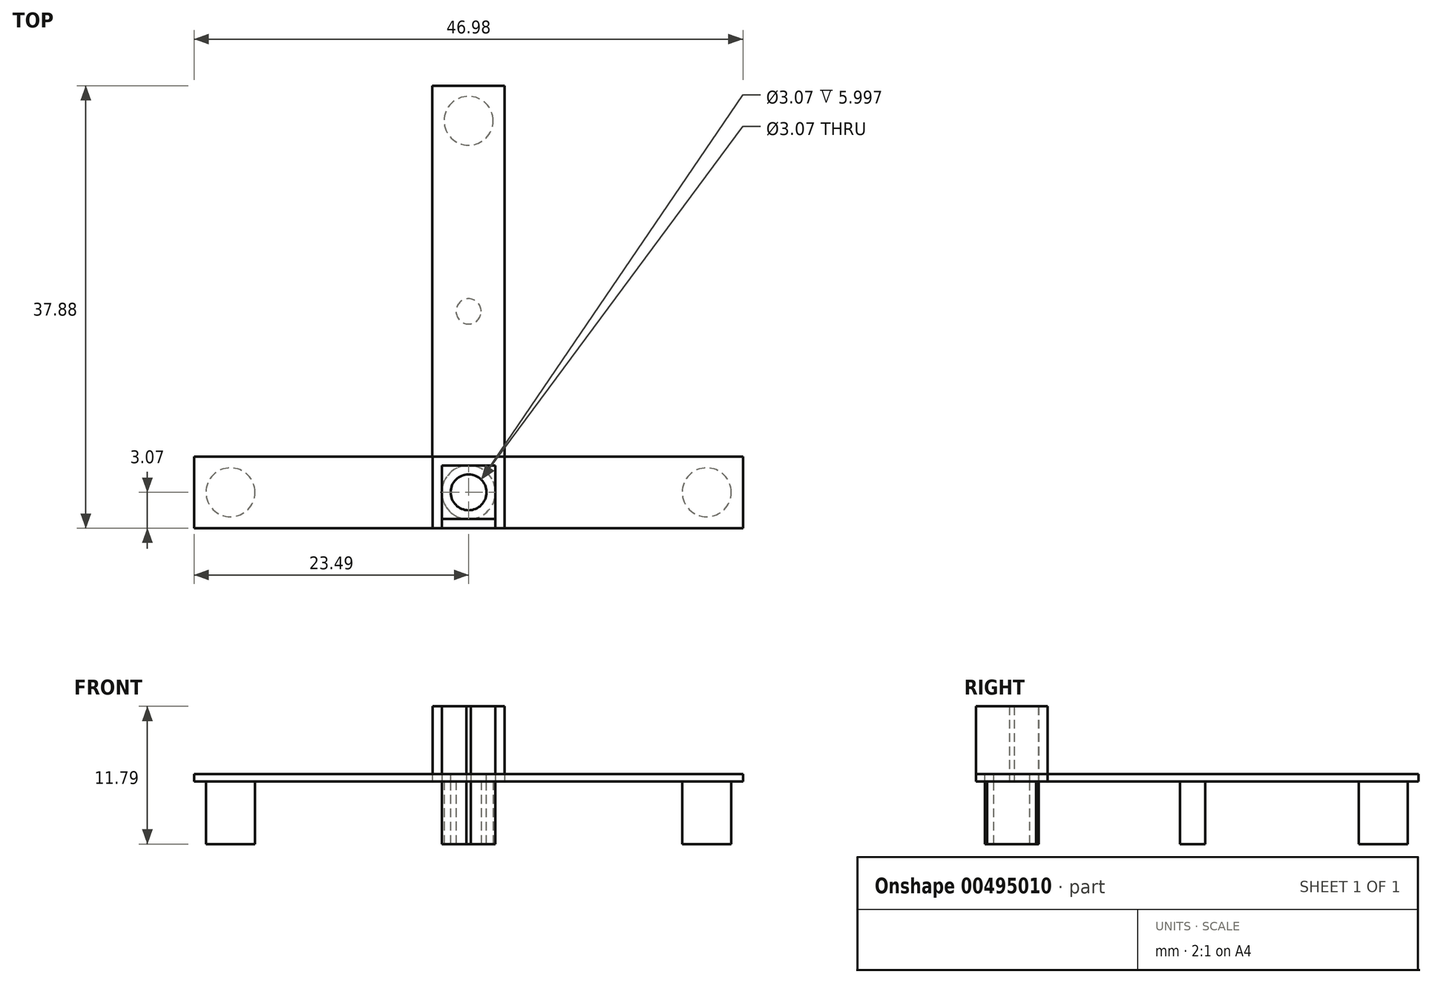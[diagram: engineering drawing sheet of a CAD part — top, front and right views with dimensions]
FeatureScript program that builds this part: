
annotation { "Feature Type Name" : "Feature", "Feature Type Description" : "" }
export const myFeature = defineFeature(function(context is Context, id is Id, definition is map)
    precondition{}
    {
        {
            var Q0;
            Q0=qCreatedBy(makeId("Top.planeOp"),FACE);
            var sketch = newSketch(context, id + "F0", { "sketchPlane" : qUnion([Q0])});
            skCircle(sketch, "E0", {"center": v(0, 0) * mm, "radius": 1.52 * mm});
            skCircle(sketch, "E1", {"center": v(0, 0) * mm, "radius": 2.3 * mm});
            skSolve(sketch);
        }
        {
            var Q0;
            Q0 = qSketchRegion(id + "F0", true);
            extrude(context, id + "F1", {"entities" : qUnion([Q0]), "depth" : 6 * mm});
        }
        {
            var Q0;
            Q0=makeQuery(id+"F1.opExtrude","CAP_FACE",FACE,{"disambiguationData":[OSD([sQuery(id+"F0.wireOp",EDGE,"E0"),sQuery(id+"F0.wireOp",EDGE,"E1")])],"isStart":false});
            var sketch = newSketch(context, id + "F2", { "sketchPlane" : qUnion([Q0])});
            skPoint(sketch, "E2.middle", {"position": v(0, 0) * mm});
            skLineSegment(sketch, "E3.bottom", {"start": v(2.3, 2.3) * mm, "end": v(-2.3, 2.3) * mm});
            skLineSegment(sketch, "E3.top", {"start": v(2.3, -2.3) * mm, "end": v(-2.3, -2.3) * mm});
            skLineSegment(sketch, "E3.left", {"start": v(2.3, 2.3) * mm, "end": v(2.3, -2.3) * mm});
            skLineSegment(sketch, "E3.right", {"start": v(-2.3, 2.3) * mm, "end": v(-2.3, -2.3) * mm});
            skCircle(sketch, "E4", {"center": v(0, 0) * mm, "radius": 1.52 * mm});
            skSolve(sketch);
        }
        {
            var Q0;
            Q0 = qSketchRegion(id + "F2", true);
            extrude(context, id + "F3", {"entities" : qUnion([Q0]), "operationType" : NewBodyOperationType.ADD, "oppositeDirection" : true, "depth" : 0.64 * mm});
        }
        {
            var Q0;
            Q0=makeQuery(id+"F3.boolean.opBoolean","MERGE",FACE,{"derivedFrom":[makeQuery(id+"F1.opExtrude","CAP_FACE",FACE,{"disambiguationData":[OSD([sQuery(id+"F0.wireOp",EDGE,"E0"),sQuery(id+"F0.wireOp",EDGE,"E1")])],"isStart":false}),makeQuery(id+"F3.opExtrude","CAP_FACE",FACE,{"disambiguationData":[OSD([sQuery(id+"F2.wireOp",EDGE,"E3.bottom"),sQuery(id+"F2.wireOp",EDGE,"E3.top"),sQuery(id+"F2.wireOp",EDGE,"E3.left"),sQuery(id+"F2.wireOp",EDGE,"E3.right"),sQuery(id+"F2.wireOp",EDGE,"E4")])],"isStart":true})]});
            var sketch = newSketch(context, id + "F4", { "sketchPlane" : qUnion([Q0])});
            skLineSegment(sketch, "E5.bottom", {"start": v(2.3, 2.3) * mm, "end": v(-2.3, 2.3) * mm});
            skLineSegment(sketch, "E5.top", {"start": v(2.3, -2.3) * mm, "end": v(-2.3, -2.3) * mm});
            skLineSegment(sketch, "E5.left", {"start": v(2.3, 2.3) * mm, "end": v(2.3, -2.3) * mm});
            skLineSegment(sketch, "E5.right", {"start": v(-2.3, 2.3) * mm, "end": v(-2.3, -2.3) * mm});
            skPoint(sketch, "E5.middle", {"position": v(0, 0) * mm});
            skLineSegment(sketch, "E6.bottom", {"start": v(3.07, 3.07) * mm, "end": v(-3.07, 3.07) * mm});
            skLineSegment(sketch, "E6.top", {"start": v(3.07, -3.07) * mm, "end": v(-3.07, -3.07) * mm});
            skLineSegment(sketch, "E6.left", {"start": v(3.07, 3.07) * mm, "end": v(3.07, -3.07) * mm});
            skLineSegment(sketch, "E6.right", {"start": v(-3.07, 3.07) * mm, "end": v(-3.07, -3.07) * mm});
            skSolve(sketch);
        }
        {
            var Q0;
            Q0=makeQuery(id+"F4.imprint","IMPRINT",FACE,{"disambiguationData":[TD([[makeQuery(id+"F4.imprint","IMPRINT",EDGE,{"derivedFrom":sQuery(id+"F4.wireOp",EDGE,"E6.bottom")}),1.0]])]});
            extrude(context, id + "F5", {"entities" : qUnion([Q0]), "depth" : 5.8 * mm});
        }
        {
            var Q0;
            Q0=makeQuery(id+"F5.opExtrude","CAP_FACE",FACE,{"disambiguationData":[OSD([sQuery(id+"F0.wireOp",EDGE,"E1"),sQuery(id+"F4.wireOp",EDGE,"E5.bottom"),sQuery(id+"F4.wireOp",EDGE,"E5.top"),sQuery(id+"F4.wireOp",EDGE,"E5.left"),sQuery(id+"F4.wireOp",EDGE,"E5.right"),sQuery(id+"F4.wireOp",EDGE,"E6.bottom"),sQuery(id+"F4.wireOp",EDGE,"E6.top"),sQuery(id+"F4.wireOp",EDGE,"E6.left"),sQuery(id+"F4.wireOp",EDGE,"E6.right")])],"isStart":false});
            var sketch = newSketch(context, id + "F6", { "sketchPlane" : qUnion([Q0])});
            skLineSegment(sketch, "E7.bottom", {"start": v(-2.3, -2.3) * mm, "end": v(2.29, -2.3) * mm});
            skLineSegment(sketch, "E7.top", {"start": v(-2.3, -4.61) * mm, "end": v(2.29, -4.61) * mm});
            skLineSegment(sketch, "E7.left", {"start": v(-2.3, -2.3) * mm, "end": v(-2.3, -4.61) * mm});
            skLineSegment(sketch, "E7.right", {"start": v(2.29, -2.3) * mm, "end": v(2.29, -4.61) * mm});
            skSolve(sketch);
        }
        {
            var Q0;
            Q0 = qSketchRegion(id + "F6", true);
            extrude(context, id + "F7", {"entities" : qUnion([Q0]), "operationType" : NewBodyOperationType.REMOVE, "oppositeDirection" : true, "depth" : 25.4 * mm});
        }
        {
            var Q0;
            Q0=makeQuery(id+"F3.boolean.opBoolean","MERGE",FACE,{"derivedFrom":[makeQuery(id+"F1.opExtrude","CAP_FACE",FACE,{"disambiguationData":[OSD([sQuery(id+"F0.wireOp",EDGE,"E0"),sQuery(id+"F0.wireOp",EDGE,"E1")])],"isStart":false}),makeQuery(id+"F3.opExtrude","CAP_FACE",FACE,{"disambiguationData":[OSD([sQuery(id+"F2.wireOp",EDGE,"E3.bottom"),sQuery(id+"F2.wireOp",EDGE,"E3.top"),sQuery(id+"F2.wireOp",EDGE,"E3.left"),sQuery(id+"F2.wireOp",EDGE,"E3.right"),sQuery(id+"F2.wireOp",EDGE,"E4")])],"isStart":true})]});
            var sketch = newSketch(context, id + "F8", { "sketchPlane" : qUnion([Q0])});
            skLineSegment(sketch, "E8.bottom", {"start": v(23.5, 3.06) * mm, "end": v(-23.5, 3.06) * mm});
            skLineSegment(sketch, "E8.top", {"start": v(23.5, -3.06) * mm, "end": v(-23.5, -3.06) * mm});
            skLineSegment(sketch, "E8.left", {"start": v(23.5, 3.06) * mm, "end": v(23.5, -3.06) * mm});
            skLineSegment(sketch, "E8.right", {"start": v(-23.5, 3.06) * mm, "end": v(-23.5, -3.06) * mm});
            skPoint(sketch, "E8.middle", {"position": v(0, 0) * mm});
            skSolve(sketch);
        }
        {
            var Q0;
            Q0 = qSketchRegion(id + "F8", true);
            extrude(context, id + "F9", {"entities" : qUnion([Q0]), "oppositeDirection" : true, "depth" : 0.64 * mm});
        }
        {
            var Q0;
            Q0=makeQuery(id+"F9.opExtrude","CAP_FACE",FACE,{"disambiguationData":[OSD([sQuery(id+"F8.wireOp",EDGE,"E8.bottom"),sQuery(id+"F8.wireOp",EDGE,"E8.top"),sQuery(id+"F8.wireOp",EDGE,"E8.left"),sQuery(id+"F8.wireOp",EDGE,"E8.right")])],"isStart":true});
            var sketch = newSketch(context, id + "F10", { "sketchPlane" : qUnion([Q0])});
            skLineSegment(sketch, "E9.bottom", {"start": v(3.06, 34.3) * mm, "end": v(-3.06, 34.3) * mm});
            skLineSegment(sketch, "E9.top", {"start": v(3.06, -34.3) * mm, "end": v(-3.06, -34.3) * mm});
            skLineSegment(sketch, "E9.left", {"start": v(3.06, 34.3) * mm, "end": v(3.06, -34.3) * mm});
            skLineSegment(sketch, "E9.right", {"start": v(-3.06, 34.3) * mm, "end": v(-3.06, -34.3) * mm});
            skPoint(sketch, "E9.middle", {"position": v(0, 0) * mm});
            skSolve(sketch);
        }
        {
            var Q0;
            {var subQ0=sQuery(id+"F10.wireOp",EDGE,"E9.left");var subQ1=makeQuery(id+"F9.opExtrude","CAP_EDGE",EDGE,{"disambiguationData":[OSD([sQuery(id+"F8.wireOp",EDGE,"E8.bottom")])],"isStart":true});var subQ2=makeQuery(id+"F10.imprint","INTERSECT",VERTEX,{"derivedFrom":[subQ1,subQ0]});Q0=makeQuery(id+"F10.imprint","IMPRINT",FACE,{"disambiguationData":[TD([[makeQuery(id+"F10.imprint","IMPRINT",EDGE,{"disambiguationData":[TD([[subQ2,-1.0]])],"derivedFrom":subQ0}),-1.0]])]});}
            var Q1;
            {var subQ0=sQuery(id+"F10.wireOp",EDGE,"E9.bottom");Q1=makeQuery(id+"F10.imprint","IMPRINT",FACE,{"disambiguationData":[TD([[makeQuery(id+"F10.imprint","IMPRINT",EDGE,{"derivedFrom":subQ0}),1.0]])]});}
            var Q2;
            {var subQ0=sQuery(id+"F10.wireOp",EDGE,"E9.top");Q2=makeQuery(id+"F10.imprint","IMPRINT",FACE,{"disambiguationData":[TD([[makeQuery(id+"F10.imprint","IMPRINT",EDGE,{"derivedFrom":subQ0}),-1.0]])]});}
            extrude(context, id + "F11", {"entities" : qUnion([Q0, Q1, Q2]), "oppositeDirection" : true, "depth" : 0.64 * mm});
        }
        {
            var Q0;
            Q0=makeQuery(id+"F11.opExtrude","CAP_FACE",FACE,{"disambiguationData":[OSD([sQuery(id+"F10.wireOp",EDGE,"E9.bottom"),sQuery(id+"F10.wireOp",EDGE,"E9.top"),sQuery(id+"F10.wireOp",EDGE,"E9.left"),sQuery(id+"F10.wireOp",EDGE,"E9.right")])],"isStart":true});
            var sketch = newSketch(context, id + "F12", { "sketchPlane" : qUnion([Q0])});
            skLineSegment(sketch, "E10.bottom", {"start": v(-3.06, -3.07) * mm, "end": v(3.06, -3.07) * mm});
            skLineSegment(sketch, "E10.top", {"start": v(-3.06, -34.3) * mm, "end": v(3.06, -34.3) * mm});
            skLineSegment(sketch, "E10.left", {"start": v(-3.06, -3.07) * mm, "end": v(-3.06, -34.3) * mm});
            skLineSegment(sketch, "E10.right", {"start": v(3.06, -3.07) * mm, "end": v(3.06, -34.3) * mm});
            skSolve(sketch);
        }
        {
            var Q0;
            Q0 = qSketchRegion(id + "F12", true);
            extrude(context, id + "F13", {"entities" : qUnion([Q0]), "operationType" : NewBodyOperationType.REMOVE, "oppositeDirection" : true, "depth" : 25.4 * mm});
        }
        {
            var Q0;
            Q0=makeQuery(id+"F11.opExtrude","SWEPT_BODY",BODY,{"disambiguationData":[OSD([sQuery(id+"F10.wireOp",EDGE,"E9.bottom"),sQuery(id+"F10.wireOp",EDGE,"E9.top"),sQuery(id+"F10.wireOp",EDGE,"E9.left"),sQuery(id+"F10.wireOp",EDGE,"E9.right")])]});
            deleteBodies(context, id + "F14", {"entities" : qUnion([Q0])});
        }
        {
            var Q0;
            Q0=makeQuery(id+"F9.opExtrude","SWEPT_FACE",FACE,{"disambiguationData":[OSD([sQuery(id+"F8.wireOp",EDGE,"E8.bottom")])]});
            var sketch = newSketch(context, id + "F15", { "sketchPlane" : qUnion([Q0])});
            skLineSegment(sketch, "E11.bottom", {"start": v(3.1, 6) * mm, "end": v(-3.07, 6) * mm});
            skLineSegment(sketch, "E11.top", {"start": v(3.1, 5.36) * mm, "end": v(-3.07, 5.36) * mm});
            skLineSegment(sketch, "E11.left", {"start": v(3.1, 6) * mm, "end": v(3.1, 5.36) * mm});
            skLineSegment(sketch, "E11.right", {"start": v(-3.07, 6) * mm, "end": v(-3.07, 5.36) * mm});
            skSolve(sketch);
        }
        {
            var Q0;
            Q0 = qSketchRegion(id + "F15", true);
            extrude(context, id + "F16", {"entities" : qUnion([Q0]), "depth" : 31.75 * mm});
        }
        {
            var Q0;
            Q0=makeQuery(id+"F9.opExtrude","CAP_FACE",FACE,{"disambiguationData":[OSD([sQuery(id+"F8.wireOp",EDGE,"E8.bottom"),sQuery(id+"F8.wireOp",EDGE,"E8.top"),sQuery(id+"F8.wireOp",EDGE,"E8.left"),sQuery(id+"F8.wireOp",EDGE,"E8.right")])],"isStart":true});
            var sketch = newSketch(context, id + "F17", { "sketchPlane" : qUnion([Q0])});
            skCircle(sketch, "E12", {"center": v(0, 0) * mm, "radius": 1.53 * mm});
            skSolve(sketch);
        }
        {
            var Q0;
            Q0 = qSketchRegion(id + "F17", true);
            extrude(context, id + "F18", {"entities" : qUnion([Q0]), "operationType" : NewBodyOperationType.REMOVE, "oppositeDirection" : true, "depth" : 25.4 * mm});
        }
        {
            var Q0;
            Q0=qCreatedBy(makeId("Top.planeOp"),FACE);
            var sketch = newSketch(context, id + "F19", { "sketchPlane" : qUnion([Q0])});
            skCircle(sketch, "E13", {"center": v(-20.38, 0) * mm, "radius": 2.1 * mm});
            skCircle(sketch, "E14", {"center": v(0, 31.8) * mm, "radius": 2.1 * mm});
            skCircle(sketch, "E15.MirrorC", {"center": v(20.38, 0) * mm, "radius": 2.1 * mm});
            skCircle(sketch, "E16", {"center": v(0, 15.5) * mm, "radius": 1.08 * mm});
            skSolve(sketch);
        }
        {
            var Q0;
            Q0 = qSketchRegion(id + "F19", true);
            extrude(context, id + "F20", {"entities" : qUnion([Q0]), "endBound" : BoundingType.UP_TO_NEXT, "depth" : 6.35 * mm});
        }
    });
